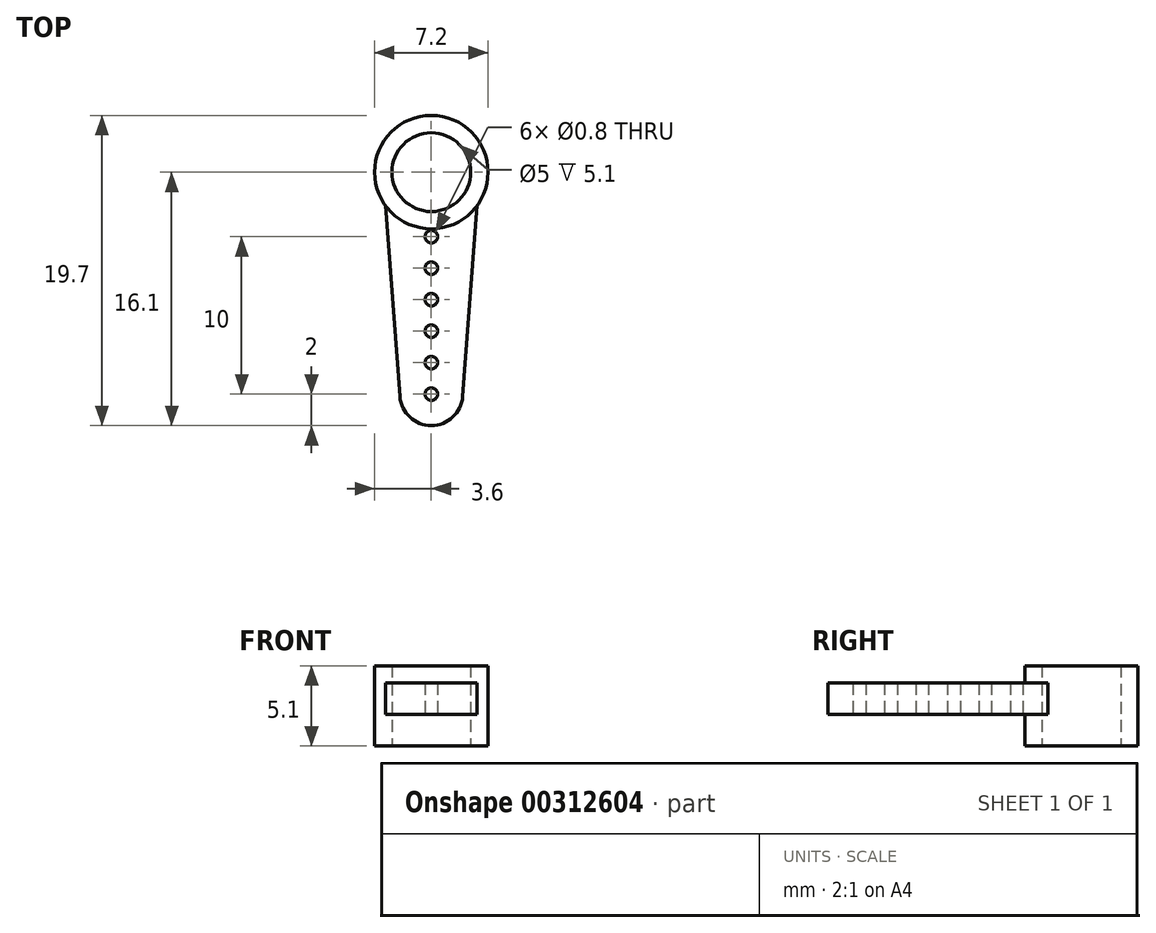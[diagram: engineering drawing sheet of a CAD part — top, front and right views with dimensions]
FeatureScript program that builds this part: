
annotation { "Feature Type Name" : "Feature", "Feature Type Description" : "" }
export const myFeature = defineFeature(function(context is Context, id is Id, definition is map)
    precondition{}
    {
        {
            var Q0;
            Q0=qCreatedBy(makeId("Top.planeOp"),FACE);
            var sketch = newSketch(context, id + "F0", { "sketchPlane" : qUnion([Q0])});
            skCircle(sketch, "E0", {"center": v(0, 0) * mm, "radius": 3.6 * mm});
            skCircle(sketch, "E1", {"center": v(0, -14.1) * mm, "radius": 2 * mm});
            skLineSegment(sketch, "E2", {"start": v(0, -16.1) * mm, "end": v(0, 3.6) * mm, "construction": true});
            skCircle(sketch, "E3", {"center": v(0, -14.1) * mm, "radius": 0.4 * mm});
            skCircle(sketch, "E4.0.1.0", {"center": v(0, -12.1) * mm, "radius": 0.4 * mm});
            skCircle(sketch, "E4.0.2.0", {"center": v(0, -10.1) * mm, "radius": 0.4 * mm});
            skCircle(sketch, "E4.0.3.0", {"center": v(0, -8.1) * mm, "radius": 0.4 * mm});
            skCircle(sketch, "E4.0.4.0", {"center": v(0, -6.1) * mm, "radius": 0.4 * mm});
            skCircle(sketch, "E4.0.5.0", {"center": v(0, -4.1) * mm, "radius": 0.4 * mm});
            skLineSegment(sketch, "E4.direction1", {"start": v(0, -14.1) * mm, "end": v(25, -14.1) * mm, "construction": true});
            skLineSegment(sketch, "E4.direction2", {"start": v(0, -14.1) * mm, "end": v(0, -12.1) * mm, "construction": true});
            skLineSegment(sketch, "E5", {"start": v(-2, -14.25) * mm, "end": v(-2.9, -2.13) * mm});
            skLineSegment(sketch, "E6", {"start": v(-2.9, -2.13) * mm, "end": v(2.9, -2.13) * mm, "construction": true});
            skLineSegment(sketch, "E7", {"start": v(2.9, -2.13) * mm, "end": v(2, -14.25) * mm});
            skCircle(sketch, "E8", {"center": v(0, 0) * mm, "radius": 2.5 * mm});
            skSolve(sketch);
        }
        {
            var Q0;
            Q0=makeQuery(id+"F0.imprint","IMPRINT",FACE,{"disambiguationData":[TD([[makeQuery(id+"F0.imprint","IMPRINT",EDGE,{"derivedFrom":sQuery(id+"F0.wireOp",EDGE,"E4.0.2.0")}),-1.0]])]});
            var Q1;
            Q1=makeQuery(id+"F0.imprint","IMPRINT",FACE,{"disambiguationData":[TD([[makeQuery(id+"F0.imprint","IMPRINT",EDGE,{"derivedFrom":sQuery(id+"F0.wireOp",EDGE,"E3")}),-1.0]])]});
            extrude(context, id + "F1", {"entities" : qUnion([Q0, Q1]), "depth" : 2 * mm});
        }
        {
            var Q0;
            Q0=makeQuery(id+"F0.imprint","IMPRINT",FACE,{"disambiguationData":[TD([[makeQuery(id+"F0.imprint","IMPRINT",EDGE,{"derivedFrom":sQuery(id+"F0.wireOp",EDGE,"E8")}),-1.0]])]});
            extrude(context, id + "F2", {"entities" : qUnion([Q0]), "operationType" : NewBodyOperationType.ADD, "depth" : 3.1 * mm, "hasSecondDirection" : true, "secondDirectionOppositeDirection" : true, "secondDirectionDepth" : 2 * mm});
        }
    });
